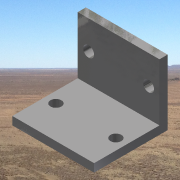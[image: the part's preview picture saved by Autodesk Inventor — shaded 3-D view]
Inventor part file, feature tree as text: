
AUTODESK INVENTOR PART (.ipt)
format: ipt  version: 2013 SP2 (Build 170200200, 200)  size: 137,216 bytes
history: native  units: in
note: dims shown in document units (in); Inventor stores cm internally (conversion verified against a paired STEP export)
features: sketch x3, hole x2, extrude x1
ambient origin geometry x8: Origin, YZ Plane, XZ Plane, XY Plane, X Axis, Y Axis, Z Axis, Center Point
bodies: Solid1 (feature_tree)
feature tree (6):
  extrude  "Extrusion1"  Depth=0.375in
  hole  "Hole1"  [1 undecoded]
  hole  "Hole2"  [1 undecoded]
  sketch  "Sketch1"  dims[d4=3.0in d5=0.375in]
  sketch  "Sketch2"  dims[d6=0.375in d7=3.0in]
  sketch  "Sketch3"  dims[d8=3.75in d9=0.0in d13=0.5in d14=2.75in d15=0.5in d16=0.75in d17=0.375in d18=0.25in d19=0.5635in d20=1.0in d21=0.8108in d22=0.5in d23=2.75in d24=0.5in d25=0.75in d26=0.375in d27=0.25in d28=0.5635in d29=1.0in d30=0.8108in]
note: 2 required parameter values undecoded (feature->parameter linkage not recoverable at this tier; creation-order binding heuristic only, values carry confidence <= 0.55)
